# Revit family: Lighting-Surface-Amerlux-Finch
name_source: partatom
category: Lighting Fixtures
units: mm (PartAtom-declared; Revit-internal decimal feet)

## family parameters
Cut with Voids When Loaded = No
Host = Face
Light Source = Yes
Part Type = Normal
Room Calculation Point = No
Round Connector Dimension = Use Diameter
Shared = No

## types (5) — shared parameters
Apparent Load = 0 VA
Color Filter = 16777215
Default Elevation = 4' - 0"
Description = Surface Mount
Dimming Lamp Color Temperature Shift = <None>
Emit Shape Visible in Rendering = No
Emit from Circle Diameter = 0' - 1 1/2"
Fixture Finish = Aluminum Finish
Manufacturer = Amerlux
Model = Finch
Number of Poles = 1
Photometric Web File = Load File
Power Factor = 1
Tilt Angle = -90.00°
URL = http://www.amerlux.com
Voltage = 0 V

## per-type parameters (varying)
| type | Fixture Length |
| FIN3-SMF | 0' - 3" |
| FIN6-SMF | 0' - 6" |
| FIN9-SMF | 0' - 9" |
| FIN12-SMF | 1' - 0" |
| FIN18-SMF | 1' - 6" |

## geometry (parser evidence)
native form markers: Sweep x3
no freeform markers — native parametric forms only
